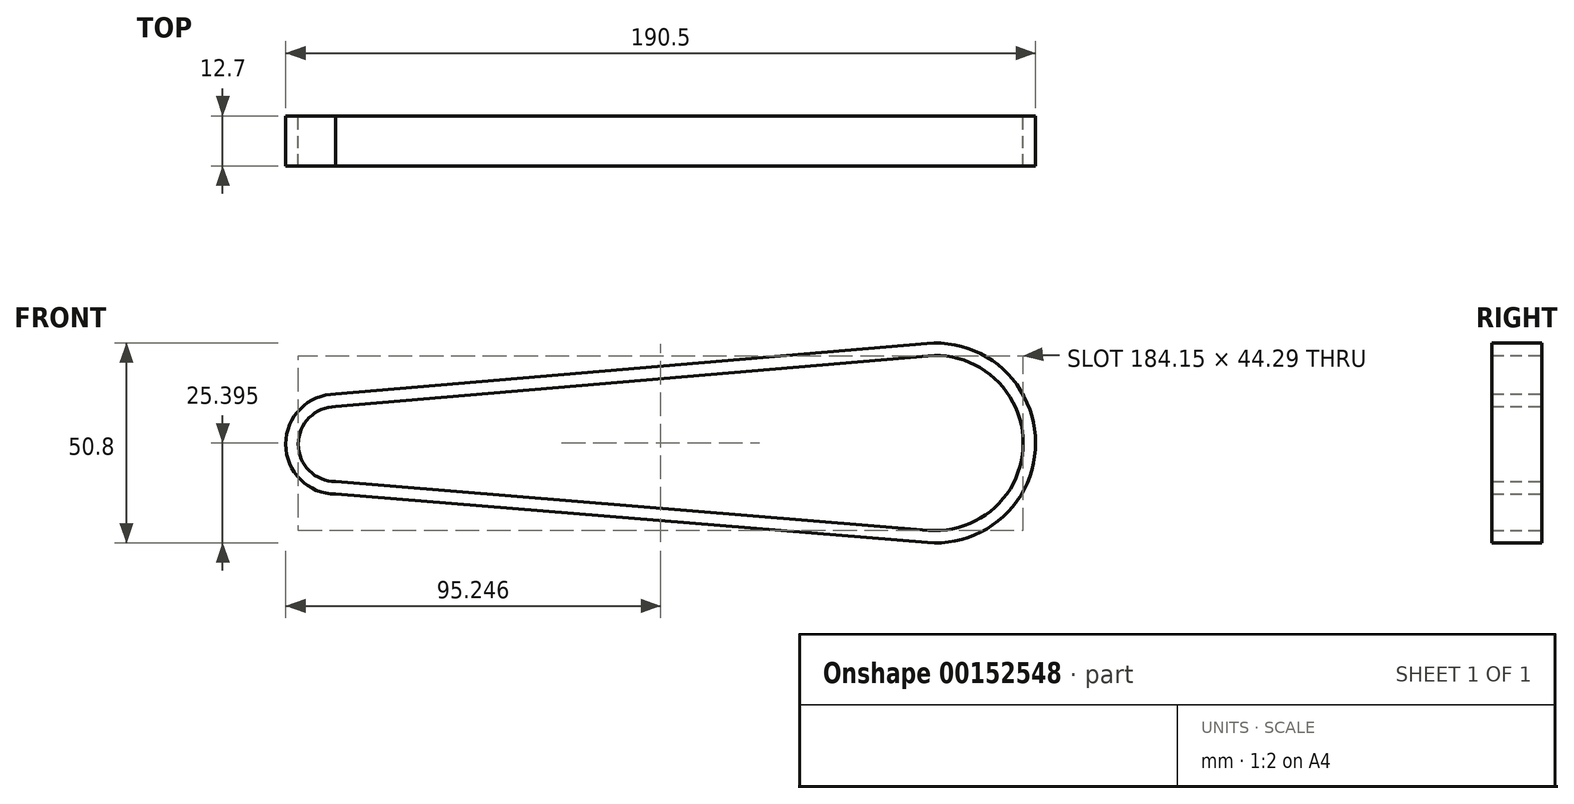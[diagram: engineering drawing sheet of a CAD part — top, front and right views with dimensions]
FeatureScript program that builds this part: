
annotation { "Feature Type Name" : "Feature", "Feature Type Description" : "" }
export const myFeature = defineFeature(function(context is Context, id is Id, definition is map)
    precondition{}
    {
        {
            var Q0;
            Q0=qCreatedBy(makeId("Front.planeOp"),FACE);
            var sketch = newSketch(context, id + "F0", { "sketchPlane" : qUnion([Q0])});
            skArc(sketch, "E0", {"start": v(-110, 14.25) * mm, "mid": v(-119.53, 4.72) * mm, "end": v(-110, -4.8) * mm});
            skArc(sketch, "E1", {"start": v(40.58, -17.13) * mm, "mid": v(64.62, 5.06) * mm, "end": v(40.5, 27.16) * mm});
            skArc(sketch, "E2", {"start": v(-110, 17.42) * mm, "mid": v(-122.7, 4.72) * mm, "end": v(-110, -7.98) * mm});
            skArc(sketch, "E3", {"start": v(40.32, -20.3) * mm, "mid": v(67.8, 5.07) * mm, "end": v(40.22, 30.33) * mm});
            skLineSegment(sketch, "E4", {"start": v(-110, 14.25) * mm, "end": v(40.5, 27.16) * mm});
            skLineSegment(sketch, "E5", {"start": v(-110, -4.8) * mm, "end": v(40.58, -17.13) * mm});
            skLineSegment(sketch, "E6", {"start": v(-110, -7.98) * mm, "end": v(40.32, -20.3) * mm});
            skLineSegment(sketch, "E7", {"start": v(-110, 17.42) * mm, "end": v(40.22, 30.33) * mm});
            skSolve(sketch);
        }
        {
            var Q0;
            Q0 = qSketchRegion(id + "F0", true);
            extrude(context, id + "F1", {"entities" : qUnion([Q0]), "depth" : 12.7 * mm});
        }
    });
